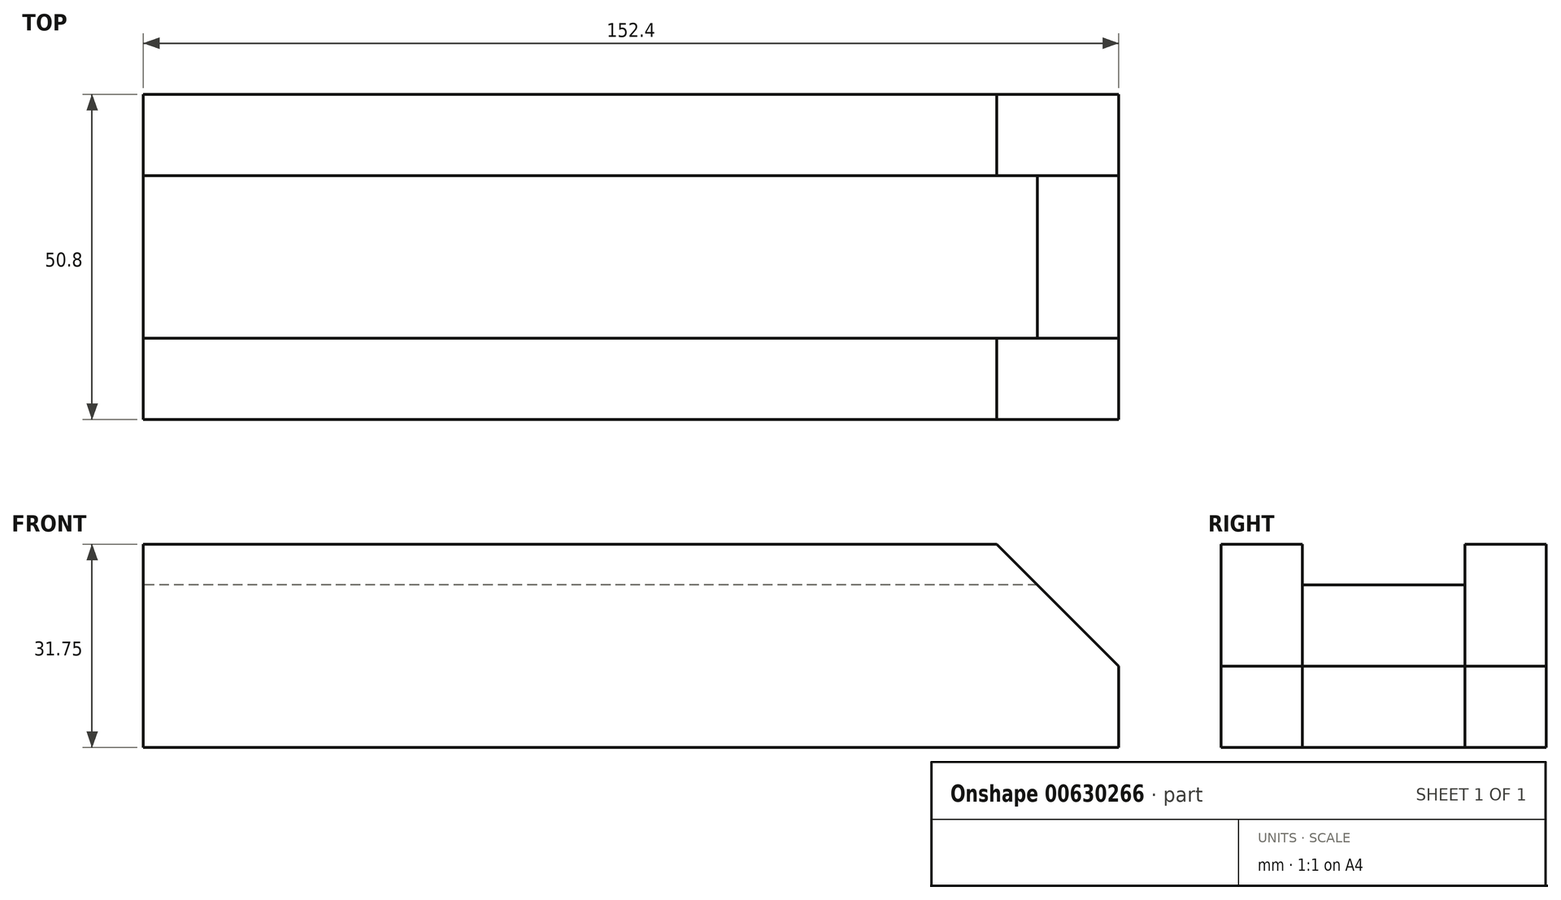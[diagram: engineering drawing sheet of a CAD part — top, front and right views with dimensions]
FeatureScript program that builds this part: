
annotation { "Feature Type Name" : "Feature", "Feature Type Description" : "" }
export const myFeature = defineFeature(function(context is Context, id is Id, definition is map)
    precondition{}
    {
        {
            var Q0;
            Q0=qCreatedBy(makeId("Right.planeOp"),FACE);
            var sketch = newSketch(context, id + "F0", { "sketchPlane" : qUnion([Q0])});
            skLineSegment(sketch, "E0.bottom", {"start": v(0, 0) * mm, "end": v(12.7, 0) * mm});
            skLineSegment(sketch, "E0.top", {"start": v(0, 31.75) * mm, "end": v(12.7, 31.75) * mm});
            skLineSegment(sketch, "E0.left", {"start": v(0, 0) * mm, "end": v(0, 31.75) * mm});
            skLineSegment(sketch, "E0.right", {"start": v(12.7, 0) * mm, "end": v(12.7, 31.75) * mm});
            skLineSegment(sketch, "E1.bottom", {"start": v(12.7, 0) * mm, "end": v(38.1, 0) * mm});
            skLineSegment(sketch, "E1.top", {"start": v(12.7, 25.4) * mm, "end": v(38.1, 25.4) * mm});
            skLineSegment(sketch, "E1.left", {"start": v(12.7, 0) * mm, "end": v(12.7, 25.4) * mm});
            skLineSegment(sketch, "E1.right", {"start": v(38.1, 0) * mm, "end": v(38.1, 25.4) * mm});
            skLineSegment(sketch, "E2.bottom", {"start": v(38.1, 0) * mm, "end": v(50.8, 0) * mm});
            skLineSegment(sketch, "E2.top", {"start": v(38.1, 31.75) * mm, "end": v(50.8, 31.75) * mm});
            skLineSegment(sketch, "E2.left", {"start": v(38.1, 0) * mm, "end": v(38.1, 31.75) * mm});
            skLineSegment(sketch, "E2.right", {"start": v(50.8, 0) * mm, "end": v(50.8, 31.75) * mm});
            skSolve(sketch);
        }
        {
            var Q0;
            Q0=makeQuery(id+"F0.imprint","IMPRINT",FACE,{"disambiguationData":[TD([[makeQuery(id+"F0.imprint","IMPRINT",EDGE,{"derivedFrom":sQuery(id+"F0.wireOp",EDGE,"E0.bottom")}),1.0]])]});
            var Q1;
            {var subQ3=sQuery(id+"F0.wireOp",EDGE,"E2.bottom");Q1=makeQuery(id+"F0.imprint","IMPRINT",FACE,{"disambiguationData":[TD([[makeQuery(id+"F0.imprint","IMPRINT",EDGE,{"derivedFrom":subQ3}),1.0]])]});}
            extrude(context, id + "F1", {"entities" : qUnion([Q0, Q1]), "depth" : 152.4 * mm, "offsetDistance" : 25.4 * mm});
        }
        {
            var Q0;
            {var subQ0=sQuery(id+"F0.wireOp",EDGE,"E1.bottom");Q0=makeQuery(id+"F0.imprint","IMPRINT",FACE,{"disambiguationData":[TD([[makeQuery(id+"F0.imprint","IMPRINT",EDGE,{"derivedFrom":subQ0}),1.0]])]});}
            var Q1;
            Q1=makeQuery(id+"F1.opExtrude","CAP_FACE",FACE,{"disambiguationData":[OSD([sQuery(id+"F0.wireOp",EDGE,"E0.bottom"),sQuery(id+"F0.wireOp",EDGE,"E0.top"),sQuery(id+"F0.wireOp",EDGE,"E0.left"),sQuery(id+"F0.wireOp",EDGE,"E0.right"),sQuery(id+"F0.wireOp",EDGE,"E1.left")])],"isStart":false});
            extrude(context, id + "F2", {"entities" : qUnion([Q0]), "endBound" : BoundingType.UP_TO_SURFACE, "depth" : 25.4 * mm, "endBoundEntityFace" : qUnion([Q1]), "offsetDistance" : 25.4 * mm});
        }
        {
            var Q0;
            Q0=makeQuery(id+"F1.opExtrude","SWEPT_FACE",FACE,{"disambiguationData":[OSD([sQuery(id+"F0.wireOp",EDGE,"E0.left")])]});
            var sketch = newSketch(context, id + "F3", { "sketchPlane" : qUnion([Q0])});
            skLineSegment(sketch, "E3", {"start": v(152.4, 12.7) * mm, "end": v(133.35, 31.75) * mm});
            skLineSegment(sketch, "E4", {"start": v(133.35, 31.75) * mm, "end": v(152.4, 31.75) * mm});
            skLineSegment(sketch, "E5", {"start": v(152.4, 31.75) * mm, "end": v(152.4, 12.7) * mm});
            skSolve(sketch);
        }
        {
            var Q0;
            Q0 = qSketchRegion(id + "F3", true);
            extrude(context, id + "F4", {"entities" : qUnion([Q0]), "operationType" : NewBodyOperationType.REMOVE, "endBound" : BoundingType.THROUGH_ALL, "oppositeDirection" : true, "depth" : 25.4 * mm, "offsetDistance" : 25.4 * mm});
        }
    });
